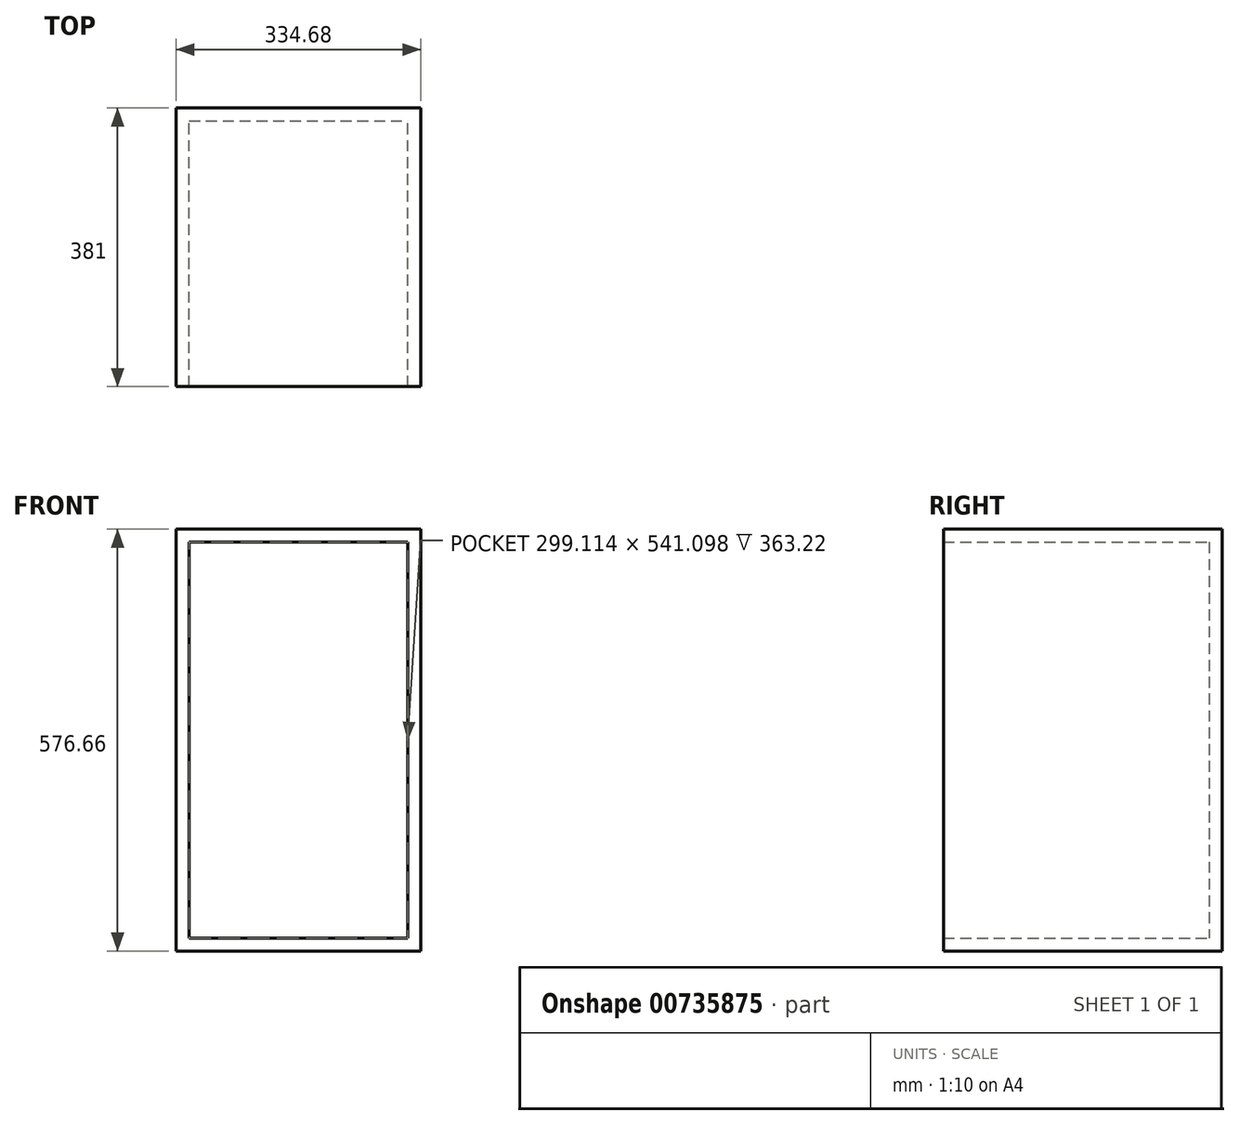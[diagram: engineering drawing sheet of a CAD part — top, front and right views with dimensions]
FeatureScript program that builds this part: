
annotation { "Feature Type Name" : "Feature", "Feature Type Description" : "" }
export const myFeature = defineFeature(function(context is Context, id is Id, definition is map)
    precondition{}
    {
        {
            var Q0;
            Q0=qCreatedBy(makeId("Front.planeOp"),FACE);
            var sketch = newSketch(context, id + "F0", { "sketchPlane" : qUnion([Q0])});
            skLineSegment(sketch, "E0.bottom", {"start": v(-27.64, 43.82) * mm, "end": v(27.64, 43.82) * mm});
            skLineSegment(sketch, "E0.top", {"start": v(-27.64, -50.24) * mm, "end": v(27.64, -50.24) * mm});
            skLineSegment(sketch, "E0.left", {"start": v(-27.64, 43.82) * mm, "end": v(-27.64, -50.24) * mm});
            skLineSegment(sketch, "E0.right", {"start": v(27.64, 43.82) * mm, "end": v(27.64, -50.24) * mm});
            skPoint(sketch, "E0.middle", {"position": v(0, -3.2) * mm});
            skSolve(sketch);
        }
        {
            var Q0;
            Q0=makeQuery(id+"F0.imprint","IMPRINT",FACE,{"disambiguationData":[TD([[makeQuery(id+"F0.imprint","IMPRINT",EDGE,{"derivedFrom":sQuery(id+"F0.wireOp",EDGE,"E0.bottom")}),-1.0]])]});
            extrude(context, id + "F1", {"entities" : qUnion([Q0]), "depth" : 381 * mm, "offsetDistance" : 25.4 * mm});
        }
        {
            var Q0;
            Q0=makeQuery(id+"F1.opExtrude","SWEPT_FACE",FACE,{"disambiguationData":[OSD([sQuery(id+"F0.wireOp",EDGE,"E0.left")])]});
            extrude(context, id + "F2", {"entities" : qUnion([Q0]), "operationType" : NewBodyOperationType.ADD, "depth" : 279.4 * mm, "offsetDistance" : 25.4 * mm});
        }
        {
            var Q0;
            {var subQ0=sQuery(id+"F0.wireOp",EDGE,"E0.bottom");Q0=makeQuery(id+"F2.boolean.opBoolean","MERGE",FACE,{"derivedFrom":[makeQuery(id+"F1.opExtrude","SWEPT_FACE",FACE,{"disambiguationData":[OSD([subQ0])]}),makeQuery(id+"F2.opExtrude","SWEPT_FACE",FACE,{"disambiguationData":[OSD([subQ0,sQuery(id+"F0.wireOp",EDGE,"E0.left")])]})]});}
            var sketch = newSketch(context, id + "F3", { "sketchPlane" : qUnion([Q0])});
            skSolve(sketch);
        }
        {
            var Q0;
            Q0 = qSketchRegion(id + "F3", true);
            var Q1;
            {var subQ0=sQuery(id+"F0.wireOp",EDGE,"E0.bottom");Q1=makeQuery(id+"F3.imprint","IMPRINT",FACE,{"disambiguationData":[TD([[makeQuery(id+"F3.imprint","IMPRINT",EDGE,{"derivedFrom":makeQuery(id+"F1.opExtrude","SWEPT_EDGE",EDGE,{"disambiguationData":[OSD([subQ0,sQuery(id+"F0.wireOp",EDGE,"E0.right")])]})}),1.0]])]});}
            extrude(context, id + "F4", {"entities" : qUnion([Q0, Q1]), "operationType" : NewBodyOperationType.ADD, "depth" : 482.6 * mm, "offsetDistance" : 25.4 * mm});
        }
        {
            var Q0;
            {var subQ0=sQuery(id+"F0.wireOp",EDGE,"E0.left");var subQ1=sQuery(id+"F0.wireOp",EDGE,"E0.bottom");Q0=makeQuery(id+"F4.boolean.opBoolean","MERGE",FACE,{"derivedFrom":[makeQuery(id+"F2.boolean.opBoolean","MERGE",FACE,{"derivedFrom":[makeQuery(id+"F1.opExtrude","CAP_FACE",FACE,{"disambiguationData":[OSD([subQ1,sQuery(id+"F0.wireOp",EDGE,"E0.top"),subQ0,sQuery(id+"F0.wireOp",EDGE,"E0.right")])],"isStart":false}),makeQuery(id+"F2.opExtrude","SWEPT_FACE",FACE,{"disambiguationData":[OSD([subQ0]),TDD([makeQuery(id+"F1.opExtrude","CAP_EDGE",EDGE,{"disambiguationData":[OSD([subQ0])],"isStart":false})])]})]}),makeQuery(id+"F4.opExtrude","SWEPT_FACE",FACE,{"disambiguationData":[OSD([subQ1,subQ0]),TDD([makeQuery(id+"F3.imprint","IMPRINT",EDGE,{"derivedFrom":makeQuery(id+"F2.boolean.opBoolean","MERGE",EDGE,{"derivedFrom":[makeQuery(id+"F1.opExtrude","CAP_EDGE",EDGE,{"disambiguationData":[OSD([subQ1])],"isStart":false}),makeQuery(id+"F2.opExtrude","SWEPT_EDGE",EDGE,{"disambiguationData":[OSD([subQ1,subQ0]),TDD([makeQuery(id+"F1.opExtrude","CAP_VERTEX",VERTEX,{"disambiguationData":[OSD([subQ1,subQ0])],"isStart":false})])]})]})})])]})]});}
            shell(context, id + "F5", {"entities" : qUnion([Q0]), "thickness" : 17.78 * mm});
        }
    });
